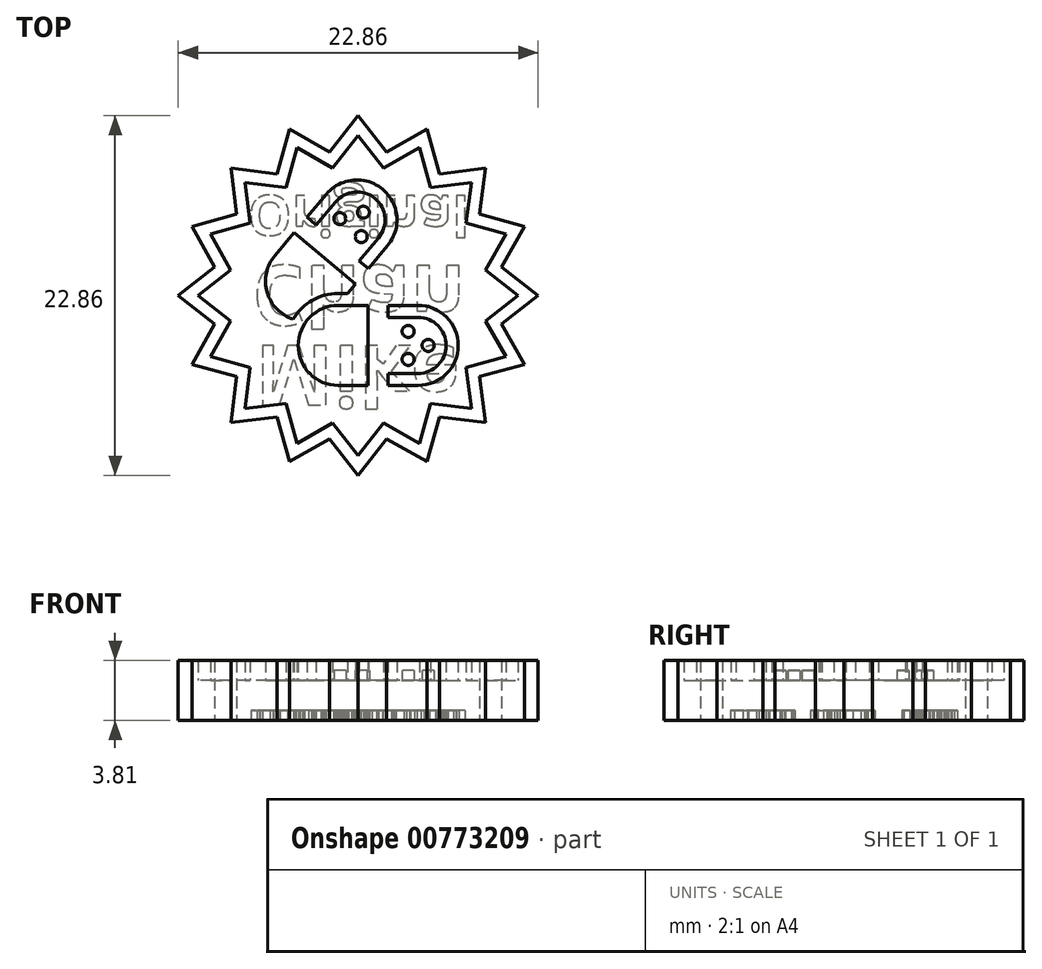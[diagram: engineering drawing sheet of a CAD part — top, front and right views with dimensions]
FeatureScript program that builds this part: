
annotation { "Feature Type Name" : "Feature", "Feature Type Description" : "" }
export const myFeature = defineFeature(function(context is Context, id is Id, definition is map)
    precondition{}
    {
        {
            var Q0;
            Q0=qCreatedBy(makeId("Top.planeOp"),FACE);
            var sketch = newSketch(context, id + "F0", { "sketchPlane" : qUnion([Q0])});
            skCircle(sketch, "E0", {"center": v(0, 0) * mm, "radius": 10.16 * mm, "construction": true});
            skLineSegment(sketch, "E1", {"start": v(0, 0) * mm, "end": v(0, 11.04) * mm, "construction": true});
            skLineSegment(sketch, "E2", {"start": v(3.89, 9.39) * mm, "end": v(0, 0) * mm, "construction": true});
            skLineSegment(sketch, "E3", {"start": v(0, 0) * mm, "end": v(1.98, 9.96) * mm, "construction": true});
            skCircle(sketch, "E4", {"center": v(0, 0) * mm, "radius": 8.26 * mm, "construction": true});
            skLineSegment(sketch, "E5.MirrorCS", {"start": v(0, 0) * mm, "end": v(5.64, 8.45) * mm, "construction": true});
            skLineSegment(sketch, "E6.MirrorCS", {"start": v(0, 0) * mm, "end": v(7.8, 7.8) * mm, "construction": true});
            skLineSegment(sketch, "E7.MirrorCS", {"start": v(0, 0) * mm, "end": v(8.45, 5.64) * mm, "construction": true});
            skLineSegment(sketch, "E8.MirrorCS", {"start": v(9.39, 3.89) * mm, "end": v(0, 0) * mm, "construction": true});
            skLineSegment(sketch, "E9.MirrorCS", {"start": v(0, 0) * mm, "end": v(9.96, 1.98) * mm, "construction": true});
            skLineSegment(sketch, "E10.MirrorCS", {"start": v(0, 0) * mm, "end": v(11.04, 0) * mm, "construction": true});
            skLineSegment(sketch, "E11.MirrorCS", {"start": v(2.54, 0) * mm, "end": v(13.58, 0) * mm, "construction": true});
            skLineSegment(sketch, "E12", {"start": v(0, 10.16) * mm, "end": v(1.61, 8.1) * mm});
            skLineSegment(sketch, "E13", {"start": v(1.61, 8.1) * mm, "end": v(3.89, 9.39) * mm});
            skLineSegment(sketch, "E14", {"start": v(3.89, 9.39) * mm, "end": v(4.59, 6.86) * mm});
            skLineSegment(sketch, "E15", {"start": v(4.59, 6.86) * mm, "end": v(7.18, 7.18) * mm});
            skLineSegment(sketch, "E16", {"start": v(7.18, 7.18) * mm, "end": v(6.86, 4.59) * mm});
            skLineSegment(sketch, "E17", {"start": v(6.86, 4.59) * mm, "end": v(9.39, 3.89) * mm});
            skLineSegment(sketch, "E18", {"start": v(9.39, 3.89) * mm, "end": v(8.1, 1.61) * mm});
            skLineSegment(sketch, "E19", {"start": v(8.1, 1.61) * mm, "end": v(10.16, 0) * mm});
            skLineSegment(sketch, "E20", {"start": v(10.16, 0) * mm, "end": v(10.16, 0) * mm});
            skLineSegment(sketch, "E21.MirrorCS", {"start": v(8.1, -1.61) * mm, "end": v(10.16, 0) * mm});
            skLineSegment(sketch, "E22.MirrorCS", {"start": v(9.39, -3.89) * mm, "end": v(8.1, -1.61) * mm});
            skLineSegment(sketch, "E23.MirrorCS", {"start": v(6.86, -4.59) * mm, "end": v(9.39, -3.89) * mm});
            skLineSegment(sketch, "E24.MirrorCS", {"start": v(7.18, -7.18) * mm, "end": v(6.86, -4.59) * mm});
            skLineSegment(sketch, "E25.MirrorCS", {"start": v(4.59, -6.86) * mm, "end": v(7.18, -7.18) * mm});
            skLineSegment(sketch, "E26.MirrorCS", {"start": v(3.89, -9.39) * mm, "end": v(4.59, -6.86) * mm});
            skLineSegment(sketch, "E27.MirrorCS", {"start": v(1.61, -8.1) * mm, "end": v(3.89, -9.39) * mm});
            skLineSegment(sketch, "E28.MirrorCS", {"start": v(0, -10.16) * mm, "end": v(1.61, -8.1) * mm});
            skLineSegment(sketch, "E29.MirrorCS", {"start": v(0, 10.16) * mm, "end": v(-1.61, 8.1) * mm});
            skLineSegment(sketch, "E30.MirrorCS", {"start": v(-1.61, 8.1) * mm, "end": v(-3.89, 9.39) * mm});
            skLineSegment(sketch, "E31.MirrorCS", {"start": v(-3.89, 9.39) * mm, "end": v(-4.59, 6.86) * mm});
            skLineSegment(sketch, "E32.MirrorCS", {"start": v(-4.59, 6.86) * mm, "end": v(-7.18, 7.18) * mm});
            skLineSegment(sketch, "E33.MirrorCS", {"start": v(-7.18, 7.18) * mm, "end": v(-6.86, 4.59) * mm});
            skLineSegment(sketch, "E34.MirrorCS", {"start": v(-6.86, 4.59) * mm, "end": v(-9.39, 3.89) * mm});
            skLineSegment(sketch, "E35.MirrorCS", {"start": v(-9.39, 3.89) * mm, "end": v(-8.1, 1.61) * mm});
            skLineSegment(sketch, "E36.MirrorCS", {"start": v(-8.1, 1.61) * mm, "end": v(-10.16, 0) * mm});
            skLineSegment(sketch, "E37.MirrorCS", {"start": v(-8.1, -1.61) * mm, "end": v(-10.16, 0) * mm});
            skLineSegment(sketch, "E38.MirrorCS", {"start": v(-9.39, -3.89) * mm, "end": v(-8.1, -1.61) * mm});
            skLineSegment(sketch, "E39.MirrorCS", {"start": v(-6.86, -4.59) * mm, "end": v(-9.39, -3.89) * mm});
            skLineSegment(sketch, "E40.MirrorCS", {"start": v(-7.18, -7.18) * mm, "end": v(-6.86, -4.59) * mm});
            skLineSegment(sketch, "E41.MirrorCS", {"start": v(-4.59, -6.86) * mm, "end": v(-7.18, -7.18) * mm});
            skLineSegment(sketch, "E42.MirrorCS", {"start": v(-3.89, -9.39) * mm, "end": v(-4.59, -6.86) * mm});
            skLineSegment(sketch, "E43.MirrorCS", {"start": v(-1.61, -8.1) * mm, "end": v(-3.89, -9.39) * mm});
            skLineSegment(sketch, "E44.MirrorCS", {"start": v(0, -10.16) * mm, "end": v(-1.61, -8.1) * mm});
            skCircle(sketch, "E45", {"center": v(0, 0) * mm, "radius": 11.43 * mm, "construction": true});
            skLineSegment(sketch, "E46", {"start": v(0, 11.43) * mm, "end": v(1.81, 9.1) * mm});
            skLineSegment(sketch, "E47.MirrorCS", {"start": v(4.37, 10.56) * mm, "end": v(1.81, 9.1) * mm});
            skLineSegment(sketch, "E48.MirrorCS", {"start": v(4.37, 10.56) * mm, "end": v(5.16, 7.72) * mm});
            skLineSegment(sketch, "E49.MirrorCS", {"start": v(8.08, 8.08) * mm, "end": v(5.16, 7.72) * mm});
            skLineSegment(sketch, "E50.MirrorCS", {"start": v(8.08, 8.08) * mm, "end": v(7.72, 5.16) * mm});
            skLineSegment(sketch, "E51.MirrorCS", {"start": v(10.56, 4.37) * mm, "end": v(7.72, 5.16) * mm});
            skLineSegment(sketch, "E52.MirrorCS", {"start": v(10.56, 4.37) * mm, "end": v(9.1, 1.81) * mm});
            skLineSegment(sketch, "E53.MirrorCS", {"start": v(11.43, 0) * mm, "end": v(9.1, 1.81) * mm});
            skLineSegment(sketch, "E54.MirrorCS", {"start": v(11.43, 0) * mm, "end": v(9.1, -1.81) * mm});
            skLineSegment(sketch, "E55.MirrorCS", {"start": v(10.56, -4.37) * mm, "end": v(9.1, -1.81) * mm});
            skLineSegment(sketch, "E56.MirrorCS", {"start": v(10.56, -4.37) * mm, "end": v(7.72, -5.16) * mm});
            skLineSegment(sketch, "E57.MirrorCS", {"start": v(8.08, -8.08) * mm, "end": v(7.72, -5.16) * mm});
            skLineSegment(sketch, "E58.MirrorCS", {"start": v(8.08, -8.08) * mm, "end": v(5.16, -7.72) * mm});
            skLineSegment(sketch, "E59.MirrorCS", {"start": v(4.37, -10.56) * mm, "end": v(5.16, -7.72) * mm});
            skLineSegment(sketch, "E60.MirrorCS", {"start": v(4.37, -10.56) * mm, "end": v(1.81, -9.1) * mm});
            skLineSegment(sketch, "E61.MirrorCS", {"start": v(0, -11.43) * mm, "end": v(1.81, -9.1) * mm});
            skLineSegment(sketch, "E62.MirrorCS", {"start": v(0, 11.43) * mm, "end": v(-1.81, 9.1) * mm});
            skLineSegment(sketch, "E63.MirrorCS", {"start": v(-4.37, 10.56) * mm, "end": v(-1.81, 9.1) * mm});
            skLineSegment(sketch, "E64.MirrorCS", {"start": v(-4.37, 10.56) * mm, "end": v(-5.16, 7.72) * mm});
            skLineSegment(sketch, "E65.MirrorCS", {"start": v(-8.08, 8.08) * mm, "end": v(-5.16, 7.72) * mm});
            skLineSegment(sketch, "E66.MirrorCS", {"start": v(-8.08, 8.08) * mm, "end": v(-7.72, 5.16) * mm});
            skLineSegment(sketch, "E67.MirrorCS", {"start": v(-10.56, 4.37) * mm, "end": v(-7.72, 5.16) * mm});
            skLineSegment(sketch, "E68.MirrorCS", {"start": v(-10.56, 4.37) * mm, "end": v(-9.1, 1.81) * mm});
            skLineSegment(sketch, "E69.MirrorCS", {"start": v(-11.43, 0) * mm, "end": v(-9.1, 1.81) * mm});
            skLineSegment(sketch, "E70.MirrorCS", {"start": v(-11.43, 0) * mm, "end": v(-9.1, -1.81) * mm});
            skLineSegment(sketch, "E71.MirrorCS", {"start": v(-10.56, -4.37) * mm, "end": v(-9.1, -1.81) * mm});
            skLineSegment(sketch, "E72.MirrorCS", {"start": v(-10.56, -4.37) * mm, "end": v(-7.72, -5.16) * mm});
            skLineSegment(sketch, "E73.MirrorCS", {"start": v(-8.08, -8.08) * mm, "end": v(-7.72, -5.16) * mm});
            skLineSegment(sketch, "E74.MirrorCS", {"start": v(-8.08, -8.08) * mm, "end": v(-5.16, -7.72) * mm});
            skLineSegment(sketch, "E75.MirrorCS", {"start": v(-4.37, -10.56) * mm, "end": v(-5.16, -7.72) * mm});
            skLineSegment(sketch, "E76.MirrorCS", {"start": v(-4.37, -10.56) * mm, "end": v(-1.81, -9.1) * mm});
            skLineSegment(sketch, "E77.MirrorCS", {"start": v(0, -11.43) * mm, "end": v(-1.81, -9.1) * mm});
            skSolve(sketch);
        }
        {
            var Q0;
            Q0 = qSketchRegion(id + "F0", true);
            extrude(context, id + "F1", {"entities" : qUnion([Q0]), "depth" : 3.8 * mm, "offsetDistance" : 25.4 * mm});
        }
        {
            var Q0;
            Q0=qCreatedBy(makeId("Top.planeOp"),FACE);
            var sketch = newSketch(context, id + "F2", { "sketchPlane" : qUnion([Q0])});
            skLineSegment(sketch, "E78", {"start": v(3.81, -3.17) * mm, "end": v(-6.04, -3.18) * mm, "construction": true});
            skArc(sketch, "E79", {"start": v(-1.27, -0.63) * mm, "mid": v(-3.81, -3.18) * mm, "end": v(-1.27, -5.72) * mm});
            skLineSegment(sketch, "E80", {"start": v(-1.27, -0.63) * mm, "end": v(0.64, -0.63) * mm});
            skLineSegment(sketch, "E81.MirrorCS", {"start": v(-1.27, -5.72) * mm, "end": v(0.64, -5.72) * mm});
            skLineSegment(sketch, "E82", {"start": v(1.27, 2.03) * mm, "end": v(1.27, -5.05) * mm, "construction": true});
            skLineSegment(sketch, "E83", {"start": v(0.64, -0.63) * mm, "end": v(0.64, -5.72) * mm});
            skLineSegment(sketch, "E84.MirrorCS", {"start": v(1.9, -0.63) * mm, "end": v(1.9, -1.4) * mm});
            skLineSegment(sketch, "E85.MirrorCS", {"start": v(3.81, -0.63) * mm, "end": v(1.9, -0.63) * mm});
            skArc(sketch, "E86.MirrorCS", {"start": v(3.81, -0.63) * mm, "mid": v(6.35, -3.18) * mm, "end": v(3.81, -5.72) * mm});
            skLineSegment(sketch, "E87.MirrorCS", {"start": v(3.81, -5.71) * mm, "end": v(1.9, -5.72) * mm});
            skArc(sketch, "E88", {"start": v(3.81, -4.95) * mm, "mid": v(5.59, -3.17) * mm, "end": v(3.81, -1.4) * mm});
            skLineSegment(sketch, "E89", {"start": v(1.9, -1.4) * mm, "end": v(3.81, -1.4) * mm});
            skLineSegment(sketch, "E90.MirrorCS", {"start": v(1.9, -4.95) * mm, "end": v(3.81, -4.95) * mm});
            skLineSegment(sketch, "E91.trimOffspring", {"start": v(1.9, -4.95) * mm, "end": v(1.9, -5.72) * mm});
            skSolve(sketch);
        }
        {
            var Q0;
            Q0=makeQuery(id+"F2.imprint","IMPRINT",FACE,{"disambiguationData":[TD([[makeQuery(id+"F2.imprint","IMPRINT",EDGE,{"derivedFrom":sQuery(id+"F2.wireOp",EDGE,"E79")}),1.0]])]});
            var Q1;
            Q1=makeQuery(id+"F2.imprint","IMPRINT",FACE,{"disambiguationData":[TD([[makeQuery(id+"F2.imprint","IMPRINT",EDGE,{"derivedFrom":sQuery(id+"F2.wireOp",EDGE,"E84.MirrorCS")}),1.0]])]});
            extrude(context, id + "F3", {"entities" : qUnion([Q0, Q1]), "operationType" : NewBodyOperationType.ADD, "depth" : 3.8 * mm, "offsetDistance" : 25.4 * mm});
        }
        {
            var Q0;
            Q0=qCreatedBy(makeId("Top.planeOp"),FACE);
            var sketch = newSketch(context, id + "F4", { "sketchPlane" : qUnion([Q0])});
            skLineSegment(sketch, "E92", {"start": v(-6.77, -3.18) * mm, "end": v(3.27, 8.78) * mm, "construction": true});
            skLineSegment(sketch, "E93", {"start": v(-8.8, 8.81) * mm, "end": v(2.1, -0.33) * mm, "construction": true});
            skArc(sketch, "E94", {"start": v(-1.27, 0.13) * mm, "mid": v(-2.91, -0.31) * mm, "end": v(-4.12, -1.51) * mm});
            skLineSegment(sketch, "E95", {"start": v(-1.27, -3.18) * mm, "end": v(4.74, -3.18) * mm, "construction": true});
            skArc(sketch, "E96", {"start": v(-5.29, 2.54) * mm, "mid": v(-5.78, 0.2) * mm, "end": v(-4.12, -1.51) * mm});
            skLineSegment(sketch, "E97", {"start": v(-5.29, 2.54) * mm, "end": v(-4.06, 4) * mm});
            skLineSegment(sketch, "E98", {"start": v(-4.06, 4) * mm, "end": v(-0.17, 0.73) * mm});
            skLineSegment(sketch, "E99.MirrorCS", {"start": v(-3.25, 4.97) * mm, "end": v(-2.66, 4.48) * mm});
            skLineSegment(sketch, "E100.MirrorCS", {"start": v(-2.02, 6.43) * mm, "end": v(-3.25, 4.97) * mm});
            skArc(sketch, "E101.MirrorCS", {"start": v(-2.02, 6.43) * mm, "mid": v(1.56, 6.74) * mm, "end": v(1.87, 3.17) * mm});
            skLineSegment(sketch, "E102.MirrorCS", {"start": v(1.87, 3.17) * mm, "end": v(0.65, 1.7) * mm});
            skPoint(sketch, "E103.orphan", {"position": v(-1.4, -0.73) * mm});
            skArc(sketch, "E104", {"start": v(1.29, 3.66) * mm, "mid": v(1.07, 6.16) * mm, "end": v(-1.44, 5.94) * mm});
            skLineSegment(sketch, "E105", {"start": v(-1.44, 5.94) * mm, "end": v(-2.66, 4.48) * mm});
            skLineSegment(sketch, "E106.MirrorCS", {"start": v(1.29, 3.66) * mm, "end": v(0.06, 2.2) * mm});
            skLineSegment(sketch, "E107.trimOffspring", {"start": v(0.06, 2.2) * mm, "end": v(0.65, 1.7) * mm});
            skPoint(sketch, "E108.MirrorCS.end.orphan", {"position": v(-0.17, 0.73) * mm});
            skLineSegment(sketch, "E109", {"start": v(-1.27, 0.13) * mm, "end": v(-0.68, 0.13) * mm});
            skLineSegment(sketch, "E110", {"start": v(-0.17, 0.73) * mm, "end": v(-0.68, 0.13) * mm});
            skSolve(sketch);
        }
        {
            var Q0;
            Q0=makeQuery(id+"F4.imprint","IMPRINT",FACE,{"disambiguationData":[TD([[makeQuery(id+"F4.imprint","IMPRINT",EDGE,{"derivedFrom":sQuery(id+"F4.wireOp",EDGE,"E94")}),-1.0]])]});
            var Q1;
            Q1=makeQuery(id+"F4.imprint","IMPRINT",FACE,{"disambiguationData":[TD([[makeQuery(id+"F4.imprint","IMPRINT",EDGE,{"derivedFrom":sQuery(id+"F4.wireOp",EDGE,"E99.MirrorCS")}),1.0]])]});
            extrude(context, id + "F5", {"entities" : qUnion([Q0, Q1]), "operationType" : NewBodyOperationType.ADD, "depth" : 3.8 * mm, "offsetDistance" : 25.4 * mm});
        }
        {
            var Q0;
            {var subQ0=sQuery(id+"F0.wireOp",EDGE,"E77.MirrorCS");var subQ1=sQuery(id+"F0.wireOp",EDGE,"E76.MirrorCS");var subQ2=sQuery(id+"F0.wireOp",EDGE,"E75.MirrorCS");var subQ3=sQuery(id+"F0.wireOp",EDGE,"E74.MirrorCS");var subQ4=sQuery(id+"F0.wireOp",EDGE,"E73.MirrorCS");var subQ5=sQuery(id+"F0.wireOp",EDGE,"E72.MirrorCS");var subQ6=sQuery(id+"F0.wireOp",EDGE,"E71.MirrorCS");var subQ7=sQuery(id+"F0.wireOp",EDGE,"E70.MirrorCS");var subQ8=sQuery(id+"F0.wireOp",EDGE,"E69.MirrorCS");var subQ9=sQuery(id+"F0.wireOp",EDGE,"E68.MirrorCS");var subQ10=sQuery(id+"F0.wireOp",EDGE,"E67.MirrorCS");var subQ11=sQuery(id+"F0.wireOp",EDGE,"E66.MirrorCS");var subQ12=sQuery(id+"F0.wireOp",EDGE,"E65.MirrorCS");var subQ13=sQuery(id+"F0.wireOp",EDGE,"E64.MirrorCS");var subQ14=sQuery(id+"F0.wireOp",EDGE,"E46");var subQ15=sQuery(id+"F0.wireOp",EDGE,"E63.MirrorCS");var subQ16=sQuery(id+"F0.wireOp",EDGE,"E62.MirrorCS");var subQ17=sQuery(id+"F0.wireOp",EDGE,"E61.MirrorCS");var subQ18=sQuery(id+"F0.wireOp",EDGE,"E60.MirrorCS");var subQ19=sQuery(id+"F0.wireOp",EDGE,"E59.MirrorCS");var subQ20=sQuery(id+"F0.wireOp",EDGE,"E58.MirrorCS");var subQ21=sQuery(id+"F0.wireOp",EDGE,"E57.MirrorCS");var subQ22=sQuery(id+"F0.wireOp",EDGE,"E56.MirrorCS");var subQ23=sQuery(id+"F0.wireOp",EDGE,"E55.MirrorCS");var subQ24=sQuery(id+"F0.wireOp",EDGE,"E54.MirrorCS");var subQ25=sQuery(id+"F0.wireOp",EDGE,"E53.MirrorCS");var subQ26=sQuery(id+"F0.wireOp",EDGE,"E52.MirrorCS");var subQ27=sQuery(id+"F0.wireOp",EDGE,"E51.MirrorCS");var subQ28=sQuery(id+"F0.wireOp",EDGE,"E50.MirrorCS");var subQ29=sQuery(id+"F0.wireOp",EDGE,"E49.MirrorCS");var subQ30=sQuery(id+"F0.wireOp",EDGE,"E48.MirrorCS");var subQ31=sQuery(id+"F0.wireOp",EDGE,"E47.MirrorCS");Q0=makeQuery(id+"FHk8Lg7og5YKldc_1.boolean.opBoolean","MERGE",FACE,{"derivedFrom":[makeQuery(id+"F1.opExtrude","CAP_FACE",FACE,{"disambiguationData":[OSD([sQuery(id+"F0.wireOp",EDGE,"E12"),sQuery(id+"F0.wireOp",EDGE,"E13"),sQuery(id+"F0.wireOp",EDGE,"E14"),sQuery(id+"F0.wireOp",EDGE,"E15"),sQuery(id+"F0.wireOp",EDGE,"E16"),sQuery(id+"F0.wireOp",EDGE,"E17"),sQuery(id+"F0.wireOp",EDGE,"E18"),sQuery(id+"F0.wireOp",EDGE,"E19"),sQuery(id+"F0.wireOp",EDGE,"E21.MirrorCS"),sQuery(id+"F0.wireOp",EDGE,"E22.MirrorCS"),sQuery(id+"F0.wireOp",EDGE,"E23.MirrorCS"),sQuery(id+"F0.wireOp",EDGE,"E24.MirrorCS"),sQuery(id+"F0.wireOp",EDGE,"E25.MirrorCS"),sQuery(id+"F0.wireOp",EDGE,"E26.MirrorCS"),sQuery(id+"F0.wireOp",EDGE,"E27.MirrorCS"),sQuery(id+"F0.wireOp",EDGE,"E28.MirrorCS"),sQuery(id+"F0.wireOp",EDGE,"E29.MirrorCS"),sQuery(id+"F0.wireOp",EDGE,"E30.MirrorCS"),sQuery(id+"F0.wireOp",EDGE,"E31.MirrorCS"),sQuery(id+"F0.wireOp",EDGE,"E32.MirrorCS"),sQuery(id+"F0.wireOp",EDGE,"E33.MirrorCS"),sQuery(id+"F0.wireOp",EDGE,"E34.MirrorCS"),sQuery(id+"F0.wireOp",EDGE,"E35.MirrorCS"),sQuery(id+"F0.wireOp",EDGE,"E36.MirrorCS"),sQuery(id+"F0.wireOp",EDGE,"E37.MirrorCS"),sQuery(id+"F0.wireOp",EDGE,"E38.MirrorCS"),sQuery(id+"F0.wireOp",EDGE,"E39.MirrorCS"),sQuery(id+"F0.wireOp",EDGE,"E40.MirrorCS"),sQuery(id+"F0.wireOp",EDGE,"E41.MirrorCS"),sQuery(id+"F0.wireOp",EDGE,"E42.MirrorCS"),sQuery(id+"F0.wireOp",EDGE,"E43.MirrorCS"),sQuery(id+"F0.wireOp",EDGE,"E44.MirrorCS"),subQ31,subQ30,subQ29,subQ28,subQ27,subQ26,subQ25,subQ24,subQ23,subQ22,subQ21,subQ20,subQ19,subQ18,subQ17,subQ16,subQ15,subQ14,subQ13,subQ12,subQ11,subQ10,subQ9,subQ8,subQ7,subQ6,subQ5,subQ4,subQ3,subQ2,subQ1,subQ0])],"isStart":true}),makeQuery(id+"FHk8Lg7og5YKldc_1.opExtrude","CAP_FACE",FACE,{"disambiguationData":[OSD([subQ31,subQ30,subQ29,subQ28,subQ27,subQ26,subQ25,subQ24,subQ23,subQ22,subQ21,subQ20,subQ19,subQ18,subQ17,subQ16,subQ15,subQ14,subQ13,subQ12,subQ11,subQ10,subQ9,subQ8,subQ7,subQ6,subQ5,subQ4,subQ3,subQ2,subQ1,subQ0])],"isStart":true})]});}
            var sketch = newSketch(context, id + "F6", { "sketchPlane" : qUnion([Q0])});
            skText(sketch, "E111", { "text": "MC", "fontName": "OpenSans-Bold.ttf"});
            skText(sketch, "E112", { "text": "Org.", "fontName": "OpenSans-Bold.ttf"});
            skLineSegment(sketch, "E113", {"start": v(0, 10.16) * mm, "end": v(0, -10.16) * mm, "construction": true});
            const initialGuessF6  = {"E111": [-0.00355, 0.00053, 1, 0, 0.00317], "E112": [-0.00465, -0.0037, 1, 0, 0.00317]};
            skSetInitialGuess(sketch, initialGuessF6);
            skSolve(sketch);
        }
        {
            var Q0;
            Q0=qSketchRegion(id+"F6",true);
            extrude(context, id + "F7", {"entities" : qUnion([Q0]), "operationType" : NewBodyOperationType.REMOVE, "oppositeDirection" : true, "depth" : 1.27 * mm, "offsetDistance" : 25.4 * mm});
        }
        {
            var Q0;
            Q0=makeQuery(id+"F0.imprint","IMPRINT",FACE,{"disambiguationData":[TD([[makeQuery(id+"F0.imprint","IMPRINT",EDGE,{"derivedFrom":sQuery(id+"F0.wireOp",EDGE,"E12")}),-1.0]])]});
            extrude(context, id + "F8", {"entities" : qUnion([Q0]), "operationType" : NewBodyOperationType.ADD, "depth" : 2.54 * mm, "offsetDistance" : 25.4 * mm});
        }
        {
            var Q0;
            {var subQ0=sQuery(id+"F0.wireOp",EDGE,"E44.MirrorCS");var subQ1=sQuery(id+"F0.wireOp",EDGE,"E43.MirrorCS");var subQ2=sQuery(id+"F0.wireOp",EDGE,"E42.MirrorCS");var subQ3=sQuery(id+"F0.wireOp",EDGE,"E41.MirrorCS");var subQ4=sQuery(id+"F0.wireOp",EDGE,"E40.MirrorCS");var subQ5=sQuery(id+"F0.wireOp",EDGE,"E39.MirrorCS");var subQ6=sQuery(id+"F0.wireOp",EDGE,"E38.MirrorCS");var subQ7=sQuery(id+"F0.wireOp",EDGE,"E37.MirrorCS");var subQ8=sQuery(id+"F0.wireOp",EDGE,"E36.MirrorCS");var subQ9=sQuery(id+"F0.wireOp",EDGE,"E35.MirrorCS");var subQ10=sQuery(id+"F0.wireOp",EDGE,"E34.MirrorCS");var subQ11=sQuery(id+"F0.wireOp",EDGE,"E33.MirrorCS");var subQ12=sQuery(id+"F0.wireOp",EDGE,"E32.MirrorCS");var subQ13=sQuery(id+"F0.wireOp",EDGE,"E31.MirrorCS");var subQ14=sQuery(id+"F0.wireOp",EDGE,"E30.MirrorCS");var subQ15=sQuery(id+"F0.wireOp",EDGE,"E29.MirrorCS");var subQ16=sQuery(id+"F0.wireOp",EDGE,"E28.MirrorCS");var subQ17=sQuery(id+"F0.wireOp",EDGE,"E27.MirrorCS");var subQ18=sQuery(id+"F0.wireOp",EDGE,"E26.MirrorCS");var subQ19=sQuery(id+"F0.wireOp",EDGE,"E25.MirrorCS");var subQ20=sQuery(id+"F0.wireOp",EDGE,"E24.MirrorCS");var subQ21=sQuery(id+"F0.wireOp",EDGE,"E23.MirrorCS");var subQ22=sQuery(id+"F0.wireOp",EDGE,"E22.MirrorCS");var subQ23=sQuery(id+"F0.wireOp",EDGE,"E21.MirrorCS");var subQ24=sQuery(id+"F0.wireOp",EDGE,"E19");var subQ25=sQuery(id+"F0.wireOp",EDGE,"E18");var subQ26=sQuery(id+"F0.wireOp",EDGE,"E17");var subQ27=sQuery(id+"F0.wireOp",EDGE,"E16");var subQ28=sQuery(id+"F0.wireOp",EDGE,"E15");var subQ29=sQuery(id+"F0.wireOp",EDGE,"E14");var subQ30=sQuery(id+"F0.wireOp",EDGE,"E13");var subQ31=sQuery(id+"F0.wireOp",EDGE,"E12");Q0=makeQuery(id+"F8.boolean.opBoolean","MERGE",FACE,{"derivedFrom":[makeQuery(id+"F1.opExtrude","CAP_FACE",FACE,{"disambiguationData":[OSD([subQ31,subQ30,subQ29,subQ28,subQ27,subQ26,subQ25,subQ24,subQ23,subQ22,subQ21,subQ20,subQ19,subQ18,subQ17,subQ16,subQ15,subQ14,subQ13,subQ12,subQ11,subQ10,subQ9,subQ8,subQ7,subQ6,subQ5,subQ4,subQ3,subQ2,subQ1,subQ0,sQuery(id+"F0.wireOp",EDGE,"E47.MirrorCS"),sQuery(id+"F0.wireOp",EDGE,"E48.MirrorCS"),sQuery(id+"F0.wireOp",EDGE,"E49.MirrorCS"),sQuery(id+"F0.wireOp",EDGE,"E50.MirrorCS"),sQuery(id+"F0.wireOp",EDGE,"E51.MirrorCS"),sQuery(id+"F0.wireOp",EDGE,"E52.MirrorCS"),sQuery(id+"F0.wireOp",EDGE,"E53.MirrorCS"),sQuery(id+"F0.wireOp",EDGE,"E54.MirrorCS"),sQuery(id+"F0.wireOp",EDGE,"E55.MirrorCS"),sQuery(id+"F0.wireOp",EDGE,"E56.MirrorCS"),sQuery(id+"F0.wireOp",EDGE,"E57.MirrorCS"),sQuery(id+"F0.wireOp",EDGE,"E58.MirrorCS"),sQuery(id+"F0.wireOp",EDGE,"E59.MirrorCS"),sQuery(id+"F0.wireOp",EDGE,"E60.MirrorCS"),sQuery(id+"F0.wireOp",EDGE,"E61.MirrorCS"),sQuery(id+"F0.wireOp",EDGE,"E62.MirrorCS"),sQuery(id+"F0.wireOp",EDGE,"E63.MirrorCS"),sQuery(id+"F0.wireOp",EDGE,"E46"),sQuery(id+"F0.wireOp",EDGE,"E64.MirrorCS"),sQuery(id+"F0.wireOp",EDGE,"E65.MirrorCS"),sQuery(id+"F0.wireOp",EDGE,"E66.MirrorCS"),sQuery(id+"F0.wireOp",EDGE,"E67.MirrorCS"),sQuery(id+"F0.wireOp",EDGE,"E68.MirrorCS"),sQuery(id+"F0.wireOp",EDGE,"E69.MirrorCS"),sQuery(id+"F0.wireOp",EDGE,"E70.MirrorCS"),sQuery(id+"F0.wireOp",EDGE,"E71.MirrorCS"),sQuery(id+"F0.wireOp",EDGE,"E72.MirrorCS"),sQuery(id+"F0.wireOp",EDGE,"E73.MirrorCS"),sQuery(id+"F0.wireOp",EDGE,"E74.MirrorCS"),sQuery(id+"F0.wireOp",EDGE,"E75.MirrorCS"),sQuery(id+"F0.wireOp",EDGE,"E76.MirrorCS"),sQuery(id+"F0.wireOp",EDGE,"E77.MirrorCS")])],"isStart":true}),makeQuery(id+"F3.opExtrude","CAP_FACE",FACE,{"disambiguationData":[OSD([sQuery(id+"F2.wireOp",EDGE,"E79"),sQuery(id+"F2.wireOp",EDGE,"E80"),sQuery(id+"F2.wireOp",EDGE,"E81.MirrorCS"),sQuery(id+"F2.wireOp",EDGE,"E83")])],"isStart":true}),makeQuery(id+"F3.opExtrude","CAP_FACE",FACE,{"disambiguationData":[OSD([sQuery(id+"F2.wireOp",EDGE,"E84.MirrorCS"),sQuery(id+"F2.wireOp",EDGE,"E85.MirrorCS"),sQuery(id+"F2.wireOp",EDGE,"E86.MirrorCS"),sQuery(id+"F2.wireOp",EDGE,"E87.MirrorCS"),sQuery(id+"F2.wireOp",EDGE,"E88"),sQuery(id+"F2.wireOp",EDGE,"E89"),sQuery(id+"F2.wireOp",EDGE,"E90.MirrorCS"),sQuery(id+"F2.wireOp",EDGE,"E91.trimOffspring")])],"isStart":true}),makeQuery(id+"F5.opExtrude","CAP_FACE",FACE,{"disambiguationData":[OSD([sQuery(id+"F4.wireOp",EDGE,"E94"),sQuery(id+"F4.wireOp",EDGE,"E96"),sQuery(id+"F4.wireOp",EDGE,"E97"),sQuery(id+"F4.wireOp",EDGE,"E108.MirrorCS"),sQuery(id+"F4.wireOp",EDGE,"E98"),sQuery(id+"F4.wireOp",EDGE,"aabfe0b5-fafb-40b7-8a96-da05c297571d.trimOffspring")])],"isStart":true}),makeQuery(id+"F5.opExtrude","CAP_FACE",FACE,{"disambiguationData":[OSD([sQuery(id+"F4.wireOp",EDGE,"E99.MirrorCS"),sQuery(id+"F4.wireOp",EDGE,"E100.MirrorCS"),sQuery(id+"F4.wireOp",EDGE,"E101.MirrorCS"),sQuery(id+"F4.wireOp",EDGE,"E102.MirrorCS"),sQuery(id+"F4.wireOp",EDGE,"E104"),sQuery(id+"F4.wireOp",EDGE,"E105"),sQuery(id+"F4.wireOp",EDGE,"E106.MirrorCS"),sQuery(id+"F4.wireOp",EDGE,"E107.trimOffspring")])],"isStart":true}),makeQuery(id+"F8.opExtrude","CAP_FACE",FACE,{"disambiguationData":[OSD([subQ31,subQ30,subQ29,subQ28,subQ27,subQ26,subQ25,subQ24,subQ23,subQ22,subQ21,subQ20,subQ19,subQ18,subQ17,subQ16,subQ15,subQ14,subQ13,subQ12,subQ11,subQ10,subQ9,subQ8,subQ7,subQ6,subQ5,subQ4,subQ3,subQ2,subQ1,subQ0])],"isStart":true})]});}
            var sketch = newSketch(context, id + "F9", { "sketchPlane" : qUnion([Q0])});
            skText(sketch, "E114", { "text": "Mike", "fontName": "OpenSans-Bold.ttf"});
            skText(sketch, "E115", { "text": "Chan", "fontName": "OpenSans-Bold.ttf"});
            skText(sketch, "E116", { "text": "Original", "fontName": "OpenSans-Bold.ttf"});
            skLineSegment(sketch, "E117", {"start": v(0, -14.9) * mm, "end": v(0, 16.18) * mm, "construction": true});
            const initialGuessF9  = {"E114": [-0.00656, 0.00318, 1, 0, 0.00381], "E115": [-0.00673, -0.0019, 1, 0, 0.00381], "E116": [-0.00702, -0.00635, 1, 0, 0.00254]};
            skSetInitialGuess(sketch, initialGuessF9);
            skSolve(sketch);
        }
        {
            var Q0;
            Q0 = qSketchRegion(id + "F9", true);
            extrude(context, id + "F10", {"entities" : qUnion([Q0]), "operationType" : NewBodyOperationType.REMOVE, "oppositeDirection" : true, "depth" : 0.64 * mm, "offsetDistance" : 25.4 * mm});
        }
        {
            var Q0;
            Q0=makeQuery(id+"F8.opExtrude","CAP_FACE",FACE,{"disambiguationData":[OSD([sQuery(id+"F0.wireOp",EDGE,"E12"),sQuery(id+"F0.wireOp",EDGE,"E13"),sQuery(id+"F0.wireOp",EDGE,"E14"),sQuery(id+"F0.wireOp",EDGE,"E15"),sQuery(id+"F0.wireOp",EDGE,"E16"),sQuery(id+"F0.wireOp",EDGE,"E17"),sQuery(id+"F0.wireOp",EDGE,"E18"),sQuery(id+"F0.wireOp",EDGE,"E19"),sQuery(id+"F0.wireOp",EDGE,"E21.MirrorCS"),sQuery(id+"F0.wireOp",EDGE,"E22.MirrorCS"),sQuery(id+"F0.wireOp",EDGE,"E23.MirrorCS"),sQuery(id+"F0.wireOp",EDGE,"E24.MirrorCS"),sQuery(id+"F0.wireOp",EDGE,"E25.MirrorCS"),sQuery(id+"F0.wireOp",EDGE,"E26.MirrorCS"),sQuery(id+"F0.wireOp",EDGE,"E27.MirrorCS"),sQuery(id+"F0.wireOp",EDGE,"E28.MirrorCS"),sQuery(id+"F0.wireOp",EDGE,"E29.MirrorCS"),sQuery(id+"F0.wireOp",EDGE,"E30.MirrorCS"),sQuery(id+"F0.wireOp",EDGE,"E31.MirrorCS"),sQuery(id+"F0.wireOp",EDGE,"E32.MirrorCS"),sQuery(id+"F0.wireOp",EDGE,"E33.MirrorCS"),sQuery(id+"F0.wireOp",EDGE,"E34.MirrorCS"),sQuery(id+"F0.wireOp",EDGE,"E35.MirrorCS"),sQuery(id+"F0.wireOp",EDGE,"E36.MirrorCS"),sQuery(id+"F0.wireOp",EDGE,"E37.MirrorCS"),sQuery(id+"F0.wireOp",EDGE,"E38.MirrorCS"),sQuery(id+"F0.wireOp",EDGE,"E39.MirrorCS"),sQuery(id+"F0.wireOp",EDGE,"E40.MirrorCS"),sQuery(id+"F0.wireOp",EDGE,"E41.MirrorCS"),sQuery(id+"F0.wireOp",EDGE,"E42.MirrorCS"),sQuery(id+"F0.wireOp",EDGE,"E43.MirrorCS"),sQuery(id+"F0.wireOp",EDGE,"E44.MirrorCS")])],"isStart":false});
            var sketch = newSketch(context, id + "F11", { "sketchPlane" : qUnion([Q0])});
            skLineSegment(sketch, "E118", {"start": v(0.64, -3.17) * mm, "end": v(5.59, -3.17) * mm, "construction": true});
            skLineSegment(sketch, "E119", {"start": v(1.9, -1.4) * mm, "end": v(1.9, -4.95) * mm, "construction": true});
            skCircle(sketch, "E120", {"center": v(3.18, -2.29) * mm, "radius": 0.38 * mm});
            skCircle(sketch, "E121", {"center": v(4.45, -3.17) * mm, "radius": 0.38 * mm});
            skLineSegment(sketch, "E122", {"start": v(4.45, -3.17) * mm, "end": v(4.45, -1.4) * mm, "construction": true});
            skCircle(sketch, "E123.MirrorC", {"center": v(3.18, -4.06) * mm, "radius": 0.38 * mm});
            skSolve(sketch);
        }
        {
            var Q0;
            Q0 = qSketchRegion(id + "F11", true);
            extrude(context, id + "F12", {"entities" : qUnion([Q0]), "operationType" : NewBodyOperationType.ADD, "depth" : 0.64 * mm, "offsetDistance" : 25.4 * mm});
        }
        {
            var Q0;
            Q0=makeQuery(id+"F8.opExtrude","CAP_FACE",FACE,{"disambiguationData":[OSD([sQuery(id+"F0.wireOp",EDGE,"E12"),sQuery(id+"F0.wireOp",EDGE,"E13"),sQuery(id+"F0.wireOp",EDGE,"E14"),sQuery(id+"F0.wireOp",EDGE,"E15"),sQuery(id+"F0.wireOp",EDGE,"E16"),sQuery(id+"F0.wireOp",EDGE,"E17"),sQuery(id+"F0.wireOp",EDGE,"E18"),sQuery(id+"F0.wireOp",EDGE,"E19"),sQuery(id+"F0.wireOp",EDGE,"E21.MirrorCS"),sQuery(id+"F0.wireOp",EDGE,"E22.MirrorCS"),sQuery(id+"F0.wireOp",EDGE,"E23.MirrorCS"),sQuery(id+"F0.wireOp",EDGE,"E24.MirrorCS"),sQuery(id+"F0.wireOp",EDGE,"E25.MirrorCS"),sQuery(id+"F0.wireOp",EDGE,"E26.MirrorCS"),sQuery(id+"F0.wireOp",EDGE,"E27.MirrorCS"),sQuery(id+"F0.wireOp",EDGE,"E28.MirrorCS"),sQuery(id+"F0.wireOp",EDGE,"E29.MirrorCS"),sQuery(id+"F0.wireOp",EDGE,"E30.MirrorCS"),sQuery(id+"F0.wireOp",EDGE,"E31.MirrorCS"),sQuery(id+"F0.wireOp",EDGE,"E32.MirrorCS"),sQuery(id+"F0.wireOp",EDGE,"E33.MirrorCS"),sQuery(id+"F0.wireOp",EDGE,"E34.MirrorCS"),sQuery(id+"F0.wireOp",EDGE,"E35.MirrorCS"),sQuery(id+"F0.wireOp",EDGE,"E36.MirrorCS"),sQuery(id+"F0.wireOp",EDGE,"E37.MirrorCS"),sQuery(id+"F0.wireOp",EDGE,"E38.MirrorCS"),sQuery(id+"F0.wireOp",EDGE,"E39.MirrorCS"),sQuery(id+"F0.wireOp",EDGE,"E40.MirrorCS"),sQuery(id+"F0.wireOp",EDGE,"E41.MirrorCS"),sQuery(id+"F0.wireOp",EDGE,"E42.MirrorCS"),sQuery(id+"F0.wireOp",EDGE,"E43.MirrorCS"),sQuery(id+"F0.wireOp",EDGE,"E44.MirrorCS")])],"isStart":false});
            var sketch = newSketch(context, id + "F13", { "sketchPlane" : qUnion([Q0])});
            skLineSegment(sketch, "E124", {"start": v(-2.12, 2.37) * mm, "end": v(1.07, 6.16) * mm, "construction": true});
            skLineSegment(sketch, "E125", {"start": v(-2.66, 4.48) * mm, "end": v(0.06, 2.2) * mm, "construction": true});
            skCircle(sketch, "E126", {"center": v(0.33, 5.28) * mm, "radius": 0.38 * mm});
            skCircle(sketch, "E127", {"center": v(-1.16, 4.88) * mm, "radius": 0.38 * mm});
            skCircle(sketch, "E128.MirrorC", {"center": v(0.2, 3.74) * mm, "radius": 0.38 * mm});
            skSolve(sketch);
        }
        {
            var Q0;
            Q0 = qSketchRegion(id + "F13", true);
            extrude(context, id + "F14", {"entities" : qUnion([Q0]), "operationType" : NewBodyOperationType.ADD, "depth" : 0.64 * mm, "offsetDistance" : 25.4 * mm});
        }
    });
